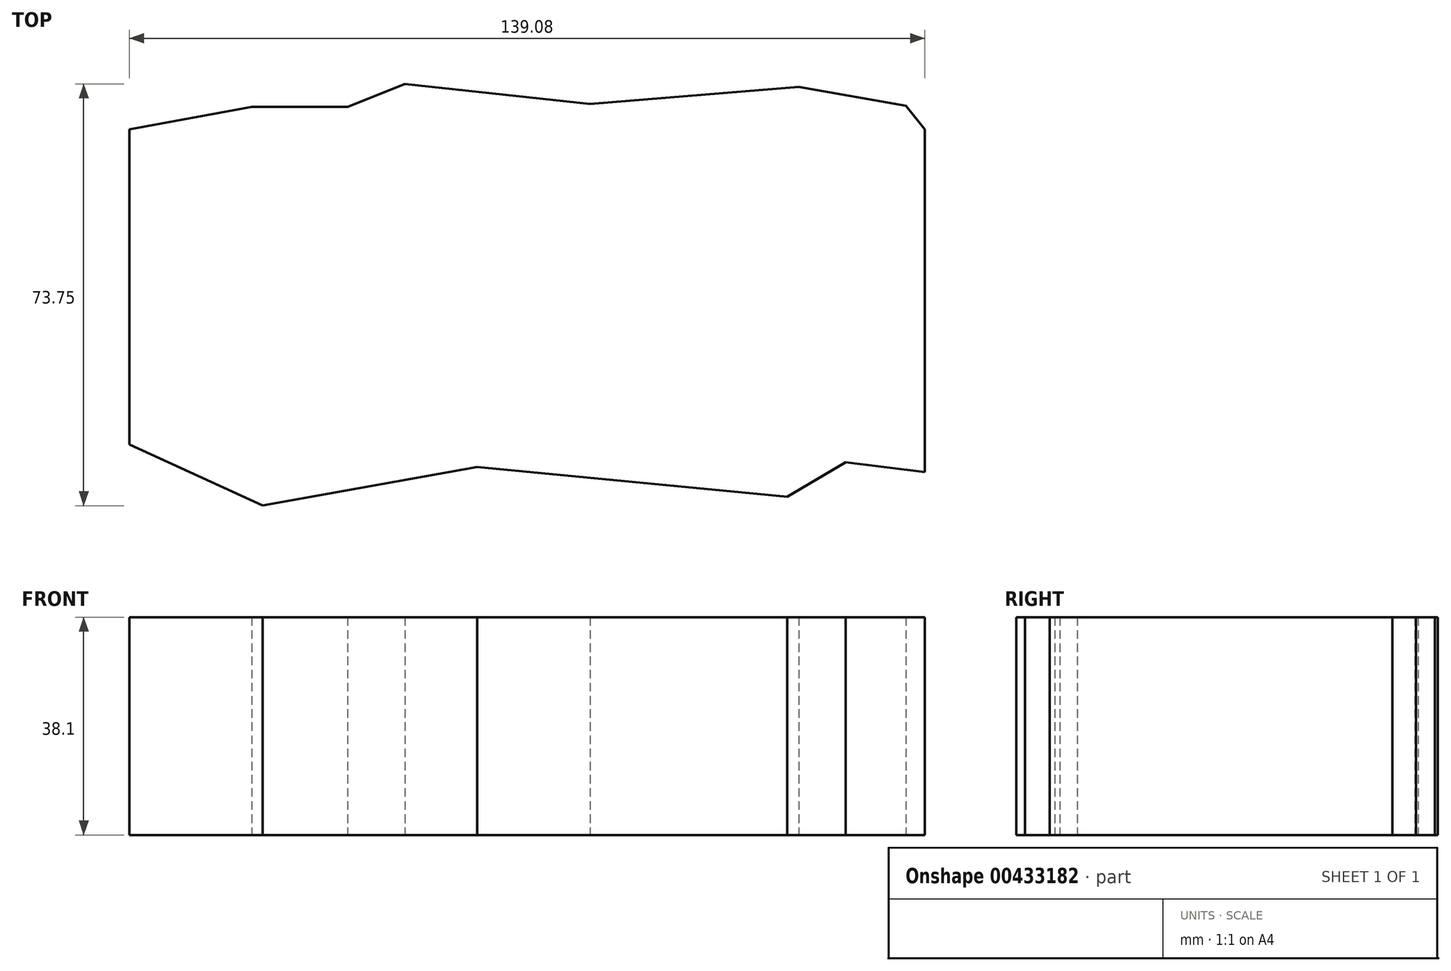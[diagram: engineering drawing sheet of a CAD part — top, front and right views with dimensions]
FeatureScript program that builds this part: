
annotation { "Feature Type Name" : "Feature", "Feature Type Description" : "" }
export const myFeature = defineFeature(function(context is Context, id is Id, definition is map)
    precondition{}
    {
        {
            var Q0;
            Q0=qCreatedBy(makeId("Top.planeOp"),FACE);
            var sketch = newSketch(context, id + "F0", { "sketchPlane" : qUnion([Q0])});
            skLineSegment(sketch, "E0.left", {"start": v(69.54, 27.55) * mm, "end": v(69.54, -27.55) * mm});
            skLineSegment(sketch, "E0.right", {"start": v(-69.54, 27.55) * mm, "end": v(-69.54, -27.55) * mm});
            skPoint(sketch, "E0.middle", {"position": v(0, 0) * mm});
            skLineSegment(sketch, "E1", {"start": v(-69.54, -27.55) * mm, "end": v(-46.28, -38.24) * mm});
            skLineSegment(sketch, "E2", {"start": v(-46.28, -38.24) * mm, "end": v(-8.7, -31.49) * mm});
            skLineSegment(sketch, "E3", {"start": v(-8.7, -31.49) * mm, "end": v(45.48, -36.68) * mm});
            skLineSegment(sketch, "E4", {"start": v(45.48, -36.68) * mm, "end": v(55.7, -30.62) * mm});
            skLineSegment(sketch, "E5", {"start": v(55.7, -30.62) * mm, "end": v(69.54, -32.35) * mm});
            skLineSegment(sketch, "E6", {"start": v(69.54, -32.35) * mm, "end": v(69.54, -27.55) * mm});
            skLineSegment(sketch, "E7", {"start": v(-69.54, 27.55) * mm, "end": v(-48.18, 31.53) * mm});
            skLineSegment(sketch, "E8", {"start": v(-48.18, 31.53) * mm, "end": v(-31.39, 31.53) * mm});
            skLineSegment(sketch, "E9", {"start": v(-31.39, 31.53) * mm, "end": v(-21.35, 35.51) * mm});
            skLineSegment(sketch, "E10", {"start": v(-21.35, 35.51) * mm, "end": v(11.03, 32.05) * mm});
            skLineSegment(sketch, "E11", {"start": v(11.03, 32.05) * mm, "end": v(47.56, 35) * mm});
            skLineSegment(sketch, "E12", {"start": v(47.56, 35) * mm, "end": v(66.25, 31.7) * mm});
            skLineSegment(sketch, "E13", {"start": v(66.25, 31.7) * mm, "end": v(69.54, 27.55) * mm});
            skSolve(sketch);
        }
        {
            var Q0;
            Q0=makeQuery(id+"F0.imprint","IMPRINT",FACE,{"disambiguationData":[TD([[makeQuery(id+"F0.imprint","IMPRINT",EDGE,{"derivedFrom":sQuery(id+"F0.wireOp",EDGE,"E0.left")}),-1.0]])]});
            extrude(context, id + "F1", {"entities" : qUnion([Q0]), "depth" : 38.1 * mm});
        }
    });
